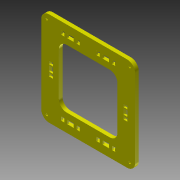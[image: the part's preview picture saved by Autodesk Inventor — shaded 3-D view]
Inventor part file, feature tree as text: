
AUTODESK INVENTOR PART (.ipt)
format: ipt  version: 2012 SP1 (Build 160190100, 190)  size: 426,496 bytes
history: native  units: in
note: dims shown in document units (in); Inventor stores cm internally (conversion verified against a paired STEP export)
features: other x4, extrude x2
ambient origin geometry x8: Origin, YZ Plane, XZ Plane, XY Plane, X Axis, Y Axis, Z Axis, Center Point
bodies: Solid1 (feature_tree)
feature tree (6):
  other  "skeleton.ipt"
  other  "POCKET_1-4"
  other  "STOCK_12MM"
  extrude  "Extrusion1"  Depth=0.3937in
  extrude  "Extrusion2"  Depth=0.4724in
  other  "THROUGH-CUT"
